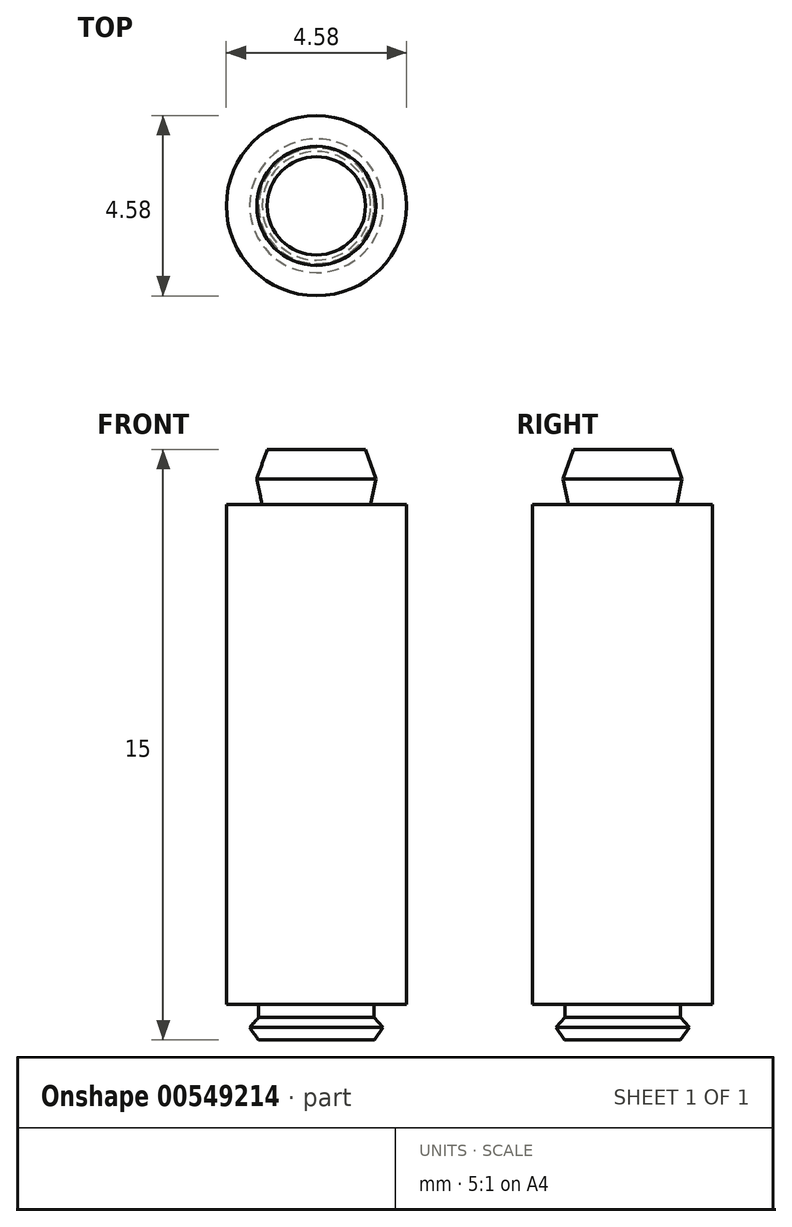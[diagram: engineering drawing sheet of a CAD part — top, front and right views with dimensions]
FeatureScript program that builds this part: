
annotation { "Feature Type Name" : "Feature", "Feature Type Description" : "" }
export const myFeature = defineFeature(function(context is Context, id is Id, definition is map)
    precondition{}
    {
        {
            var Q0;
            Q0=qCreatedBy(makeId("Front.planeOp"),FACE);
            var sketch = newSketch(context, id + "F0", { "sketchPlane" : qUnion([Q0])});
            skLineSegment(sketch, "E0", {"start": v(0, 0) * mm, "end": v(0, 14.1) * mm});
            skLineSegment(sketch, "E1", {"start": v(0, 12.7) * mm, "end": v(2.29, 12.7) * mm});
            skLineSegment(sketch, "E2", {"start": v(2.29, 12.7) * mm, "end": v(2.29, 0) * mm});
            skLineSegment(sketch, "E3", {"start": v(2.29, 0) * mm, "end": v(0, 0) * mm});
            skLineSegment(sketch, "E4", {"start": v(1.38, 12.7) * mm, "end": v(1.51, 13.35) * mm});
            skLineSegment(sketch, "E5", {"start": v(1.51, 13.35) * mm, "end": v(1.25, 14.1) * mm});
            skLineSegment(sketch, "E6", {"start": v(1.25, 14.1) * mm, "end": v(0, 14.1) * mm});
            skLineSegment(sketch, "E7", {"start": v(1.47, 0) * mm, "end": v(1.47, -0.33) * mm});
            skLineSegment(sketch, "E8", {"start": v(1.47, -0.33) * mm, "end": v(1.7, -0.59) * mm});
            skLineSegment(sketch, "E9", {"start": v(1.7, -0.59) * mm, "end": v(1.47, -0.9) * mm});
            skLineSegment(sketch, "E10", {"start": v(1.47, -0.9) * mm, "end": v(0, -0.9) * mm});
            skLineSegment(sketch, "E11", {"start": v(0, -0.9) * mm, "end": v(0, 0) * mm});
            skSolve(sketch);
        }
        {
            var Q0;
            {var subQ0=sQuery(id+"F0.wireOp",EDGE,"E4");Q0=makeQuery(id+"F0.imprint","IMPRINT",FACE,{"disambiguationData":[TD([[makeQuery(id+"F0.imprint","IMPRINT",EDGE,{"derivedFrom":subQ0}),1.0]])]});}
            var Q1;
            {var subQ0=sQuery(id+"F0.wireOp",EDGE,"E7");Q1=makeQuery(id+"F0.imprint","IMPRINT",FACE,{"disambiguationData":[TD([[makeQuery(id+"F0.imprint","IMPRINT",EDGE,{"derivedFrom":subQ0}),-1.0]])]});}
            var Q2;
            {var subQ0=sQuery(id+"F0.wireOp",EDGE,"E2");Q2=makeQuery(id+"F0.imprint","IMPRINT",FACE,{"disambiguationData":[TD([[makeQuery(id+"F0.imprint","IMPRINT",EDGE,{"derivedFrom":subQ0}),-1.0]])]});}
            var Q3;
            Q3=sQuery(id+"F0.wireOp",EDGE,"E0");
            revolve(context, id + "F1", {"entities" : qUnion([Q0, Q1, Q2]), "axis" : qUnion([Q3]), "revolveType" : RevolveType.FULL});
        }
    });
